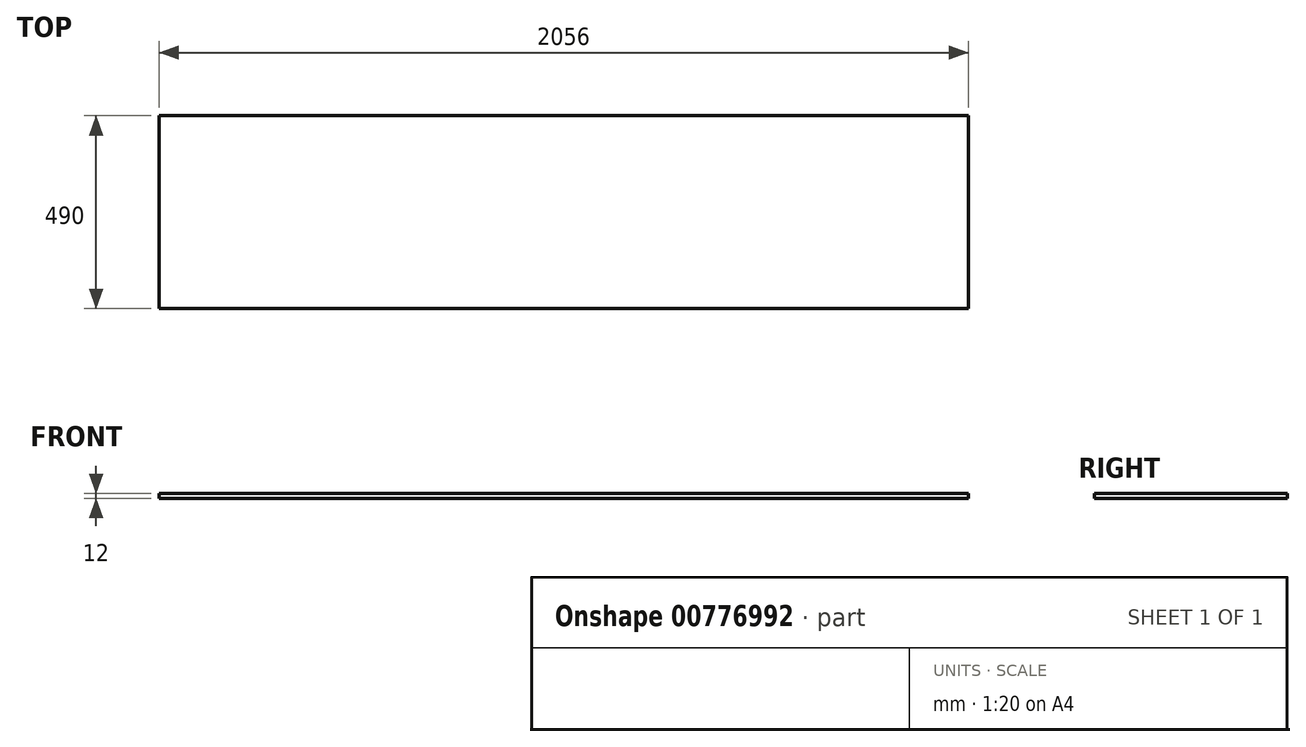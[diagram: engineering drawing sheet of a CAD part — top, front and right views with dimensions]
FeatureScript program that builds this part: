
annotation { "Feature Type Name" : "Feature", "Feature Type Description" : "" }
export const myFeature = defineFeature(function(context is Context, id is Id, definition is map)
    precondition{}
    {
        {
            var Q0;
            Q0=qCreatedBy(makeId("Top.planeOp"),FACE);
            var sketch = newSketch(context, id + "F0", { "sketchPlane" : qUnion([Q0])});
            skLineSegment(sketch, "E0.bottom", {"start": v(-1023.44, 60.06) * mm, "end": v(1032.56, 60.06) * mm});
            skLineSegment(sketch, "E0.top", {"start": v(-1023.44, -429.94) * mm, "end": v(1032.56, -429.94) * mm});
            skLineSegment(sketch, "E0.left", {"start": v(-1023.44, 60.06) * mm, "end": v(-1023.44, -429.94) * mm});
            skLineSegment(sketch, "E0.right", {"start": v(1032.56, 60.06) * mm, "end": v(1032.56, -429.94) * mm});
            skSolve(sketch);
        }
        {
            var Q0;
            Q0 = qSketchRegion(id + "F0", true);
            extrude(context, id + "F1", {"entities" : qUnion([Q0]), "depth" : 12 * mm, "offsetDistance" : 25 * mm});
        }
    });
